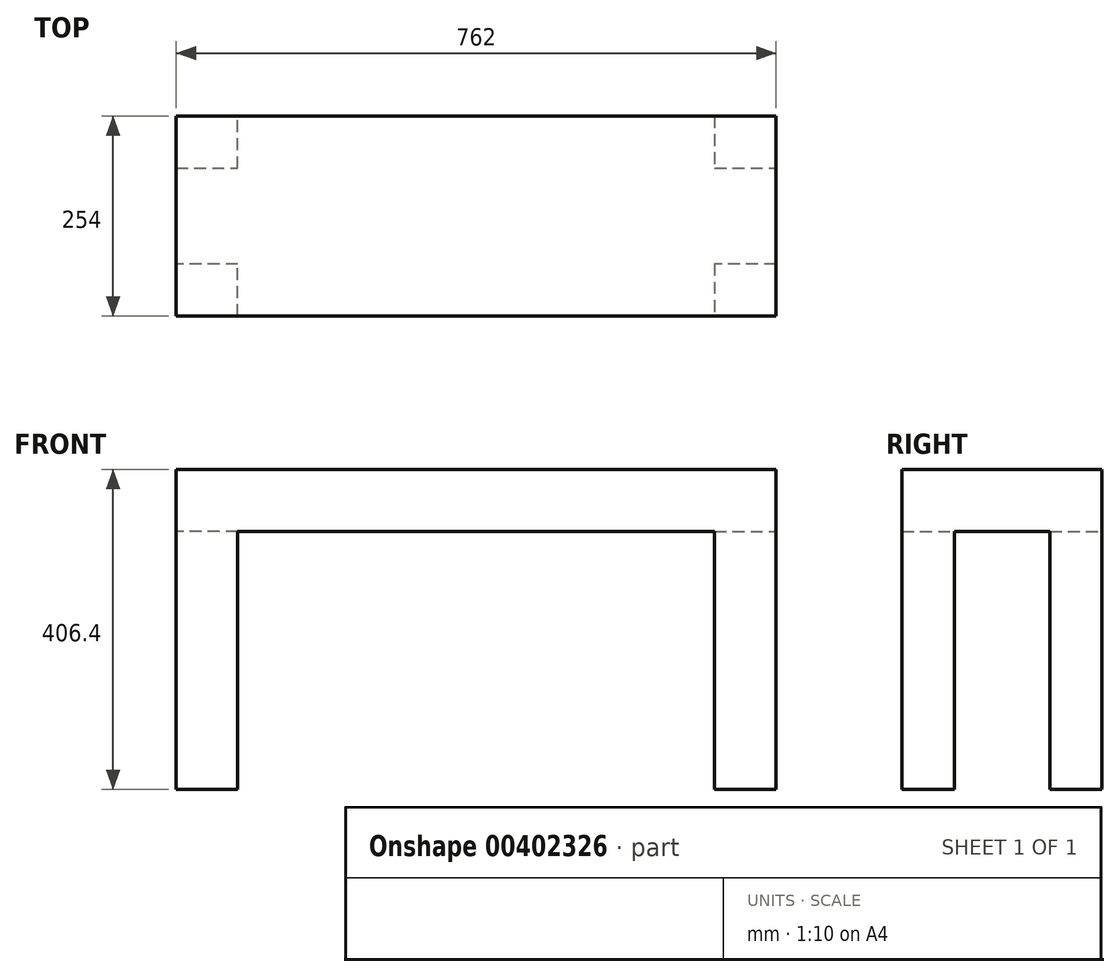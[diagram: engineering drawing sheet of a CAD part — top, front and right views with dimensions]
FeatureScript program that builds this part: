
annotation { "Feature Type Name" : "Feature", "Feature Type Description" : "" }
export const myFeature = defineFeature(function(context is Context, id is Id, definition is map)
    precondition{}
    {
        {
            var Q0;
            Q0=qCreatedBy(makeId("Top.planeOp"),FACE);
            var sketch = newSketch(context, id + "F0", { "sketchPlane" : qUnion([Q0])});
            skLineSegment(sketch, "E0.bottom", {"start": v(-381, 127) * mm, "end": v(381, 127) * mm});
            skLineSegment(sketch, "E0.top", {"start": v(-381, -127) * mm, "end": v(381, -127) * mm});
            skLineSegment(sketch, "E0.left", {"start": v(-381, 127) * mm, "end": v(-381, -127) * mm});
            skLineSegment(sketch, "E0.right", {"start": v(381, 127) * mm, "end": v(381, -127) * mm});
            skPoint(sketch, "E0.middle", {"position": v(0, 0) * mm});
            skSolve(sketch);
        }
        {
            var Q0;
            Q0 = qSketchRegion(id + "F0", true);
            extrude(context, id + "F1", {"entities" : qUnion([Q0]), "depth" : 406.4 * mm, "symmetric" : true});
        }
        {
            var Q0;
            Q0=makeQuery(id+"F1.opExtrude","CAP_FACE",FACE,{"disambiguationData":[OSD([sQuery(id+"F0.wireOp",EDGE,"E0.bottom"),sQuery(id+"F0.wireOp",EDGE,"E0.top"),sQuery(id+"F0.wireOp",EDGE,"E0.left"),sQuery(id+"F0.wireOp",EDGE,"E0.right")])],"isStart":true});
            var sketch = newSketch(context, id + "F2", { "sketchPlane" : qUnion([Q0])});
            skLineSegment(sketch, "E1", {"start": v(-302.88, 127) * mm, "end": v(-302.88, 60.74) * mm});
            skLineSegment(sketch, "E2", {"start": v(-302.88, 60.74) * mm, "end": v(-381, 60.74) * mm});
            skLineSegment(sketch, "E3", {"start": v(-381, 60.74) * mm, "end": v(-381, -60.74) * mm});
            skLineSegment(sketch, "E4", {"start": v(-381, -60.74) * mm, "end": v(-302.88, -60.74) * mm});
            skLineSegment(sketch, "E5", {"start": v(-302.88, -60.74) * mm, "end": v(-302.88, -127) * mm});
            skLineSegment(sketch, "E6", {"start": v(-302.88, -127) * mm, "end": v(302.88, -127) * mm});
            skLineSegment(sketch, "E7", {"start": v(302.88, -127) * mm, "end": v(302.88, -60.74) * mm});
            skLineSegment(sketch, "E8", {"start": v(302.88, -60.74) * mm, "end": v(381, -60.74) * mm});
            skLineSegment(sketch, "E9", {"start": v(381, -60.74) * mm, "end": v(381, 60.74) * mm});
            skLineSegment(sketch, "E10", {"start": v(381, 60.74) * mm, "end": v(302.88, 60.74) * mm});
            skLineSegment(sketch, "E11", {"start": v(302.88, 60.74) * mm, "end": v(302.88, 127) * mm});
            skLineSegment(sketch, "E12", {"start": v(302.88, 127) * mm, "end": v(-302.88, 127) * mm});
            skLineSegment(sketch, "E13", {"start": v(-381, 0) * mm, "end": v(381, 0) * mm, "construction": true});
            skLineSegment(sketch, "E14", {"start": v(0, 127) * mm, "end": v(0, -127) * mm, "construction": true});
            skSolve(sketch);
        }
        {
            var Q0;
            Q0 = qSketchRegion(id + "F2", true);
            extrude(context, id + "F3", {"entities" : qUnion([Q0]), "operationType" : NewBodyOperationType.REMOVE, "oppositeDirection" : true, "depth" : 327.66 * mm});
        }
    });
